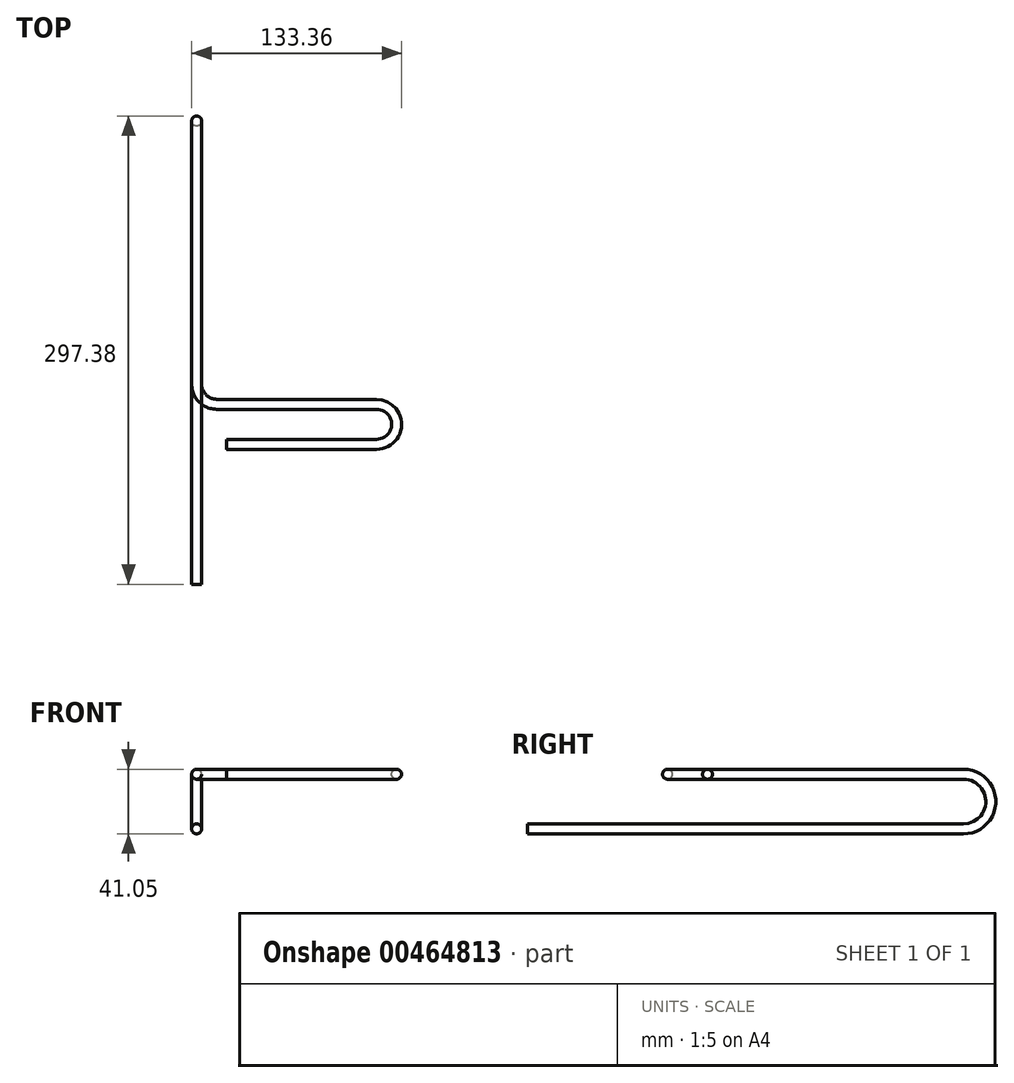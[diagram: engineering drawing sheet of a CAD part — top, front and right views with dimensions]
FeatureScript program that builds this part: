
annotation { "Feature Type Name" : "Feature", "Feature Type Description" : "" }
export const myFeature = defineFeature(function(context is Context, id is Id, definition is map)
    precondition{}
    {
        {
            var Q0;
            Q0=qCreatedBy(makeId("Right.planeOp"),FACE);
            var sketch = newSketch(context, id + "F0", { "sketchPlane" : qUnion([Q0])});
            skLineSegment(sketch, "E0", {"start": v(149.86, 0) * mm, "end": v(0, 0) * mm});
            skArc(sketch, "E1", {"start": v(149.86, -34.7) * mm, "mid": v(167.2, -17.35) * mm, "end": v(149.86, 0) * mm});
            skCircle(sketch, "E2", {"center": v(149.86, -17.35) * mm, "radius": 14.17 * mm, "construction": true});
            skLineSegment(sketch, "E3", {"start": v(149.86, -34.7) * mm, "end": v(0, -34.7) * mm});
            skSolve(sketch);
        }
        {
            var Q0;
            Q0=qCreatedBy(makeId("Top.planeOp"),FACE);
            var sketch = newSketch(context, id + "F1", { "sketchPlane" : qUnion([Q0])});
            skLineSegment(sketch, "E4", {"start": v(12.7, -12.7) * mm, "end": v(114.3, -12.7) * mm});
            skArc(sketch, "E5", {"start": v(114.3, -38.1) * mm, "mid": v(127, -25.4) * mm, "end": v(114.3, -12.7) * mm});
            skLineSegment(sketch, "E6", {"start": v(114.3, -38.1) * mm, "end": v(19.05, -38.1) * mm});
            skLineSegment(sketch, "E7", {"start": v(114.3, -12.7) * mm, "end": v(114.3, -38.1) * mm, "construction": true});
            skArc(sketch, "E8", {"start": v(0, 0) * mm, "mid": v(3.72, -8.98) * mm, "end": v(12.7, -12.7) * mm});
            skSolve(sketch);
        }
        {
            var Q0;
            Q0=qCreatedBy(makeId("Front.planeOp"),FACE);
            var sketch = newSketch(context, id + "F2", { "sketchPlane" : qUnion([Q0])});
            skCircle(sketch, "E9", {"center": v(0, -34.7) * mm, "radius": 3.18 * mm});
            skSolve(sketch);
        }
        {
            var Q0;
            Q0=makeQuery(id+"F2.imprint","IMPRINT",FACE,{"disambiguationData":[TD([[makeQuery(id+"F2.imprint","IMPRINT",EDGE,{"derivedFrom":sQuery(id+"F2.wireOp",EDGE,"E9")}),1.0]])]});
            var Q1;
            Q1=sQuery(id+"F0.wireOp",EDGE,"E3");
            var Q2;
            Q2=sQuery(id+"F0.wireOp",EDGE,"E1");
            var Q3;
            Q3=sQuery(id+"F0.wireOp",EDGE,"E0");
            var Q4;
            Q4=sQuery(id+"F1.wireOp",EDGE,"E8");
            var Q5;
            Q5=sQuery(id+"F1.wireOp",EDGE,"E4");
            var Q6;
            Q6=sQuery(id+"F1.wireOp",EDGE,"E5");
            var Q7;
            Q7=sQuery(id+"F1.wireOp",EDGE,"E6");
            sweep(context, id + "F3", {"profiles" : qUnion([Q0]), "path" : qUnion([Q1, Q2, Q3, Q4, Q5, Q6, Q7])});
        }
        {
            var Q0;
            Q0=makeQuery(id+"F3.opSweep","CAP_FACE",FACE,{"disambiguationData":[OSD([sQuery(id+"F0.wireOp",VERTEX,"E3.end"),sQuery(id+"F2.wireOp",EDGE,"E9")])],"isStart":true});
            extrude(context, id + "F4", {"entities" : qUnion([Q0]), "operationType" : NewBodyOperationType.ADD, "depth" : 127 * mm, "offsetDistance" : 25.4 * mm});
        }
    });
